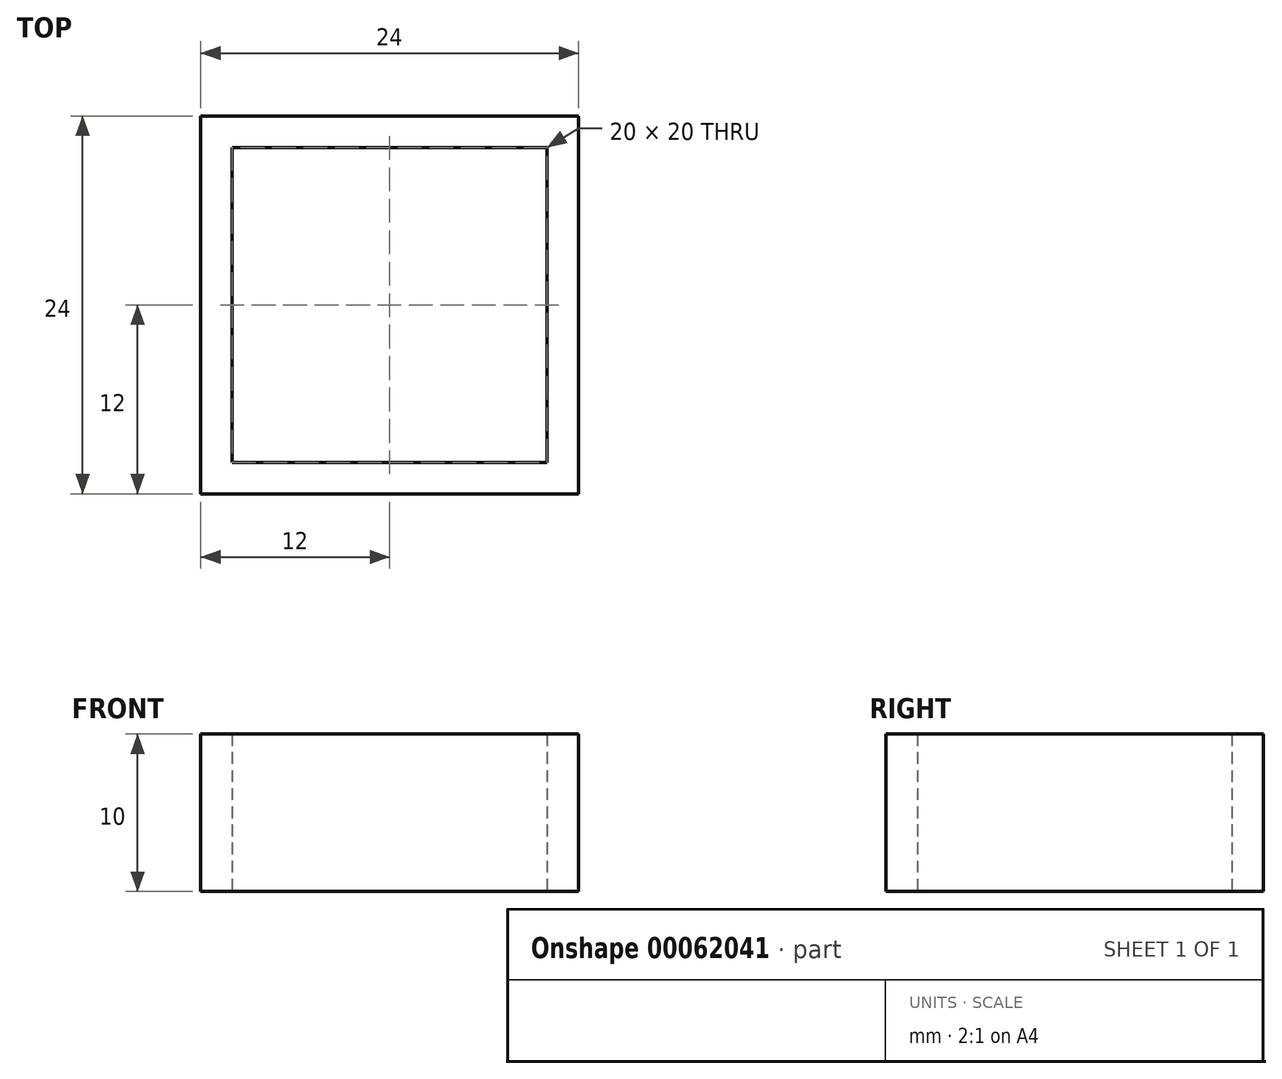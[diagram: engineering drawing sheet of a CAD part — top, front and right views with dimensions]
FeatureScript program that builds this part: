
annotation { "Feature Type Name" : "Feature", "Feature Type Description" : "" }
export const myFeature = defineFeature(function(context is Context, id is Id, definition is map)
    precondition{}
    {
        {
            var Q0;
            Q0=qCreatedBy(makeId("Top.planeOp"),FACE);
            var sketch = newSketch(context, id + "F0", { "sketchPlane" : qUnion([Q0])});
            skLineSegment(sketch, "E0.rect.bottom", {"start": v(10, -10) * mm, "end": v(-10, -10) * mm});
            skLineSegment(sketch, "E0.rect.top", {"start": v(10, 10) * mm, "end": v(-10, 10) * mm});
            skLineSegment(sketch, "E0.rect.left", {"start": v(10, -10) * mm, "end": v(10, 10) * mm});
            skLineSegment(sketch, "E0.rect.right", {"start": v(-10, -10) * mm, "end": v(-10, 10) * mm});
            skPoint(sketch, "E0.rect.middle", {"position": v(0, 0) * mm});
            skLineSegment(sketch, "E1.rect.bottom", {"start": v(12, -12) * mm, "end": v(-12, -12) * mm});
            skLineSegment(sketch, "E1.rect.top", {"start": v(12, 12) * mm, "end": v(-12, 12) * mm});
            skLineSegment(sketch, "E1.rect.left", {"start": v(12, -12) * mm, "end": v(12, 12) * mm});
            skLineSegment(sketch, "E1.rect.right", {"start": v(-12, -12) * mm, "end": v(-12, 12) * mm});
            skSolve(sketch);
        }
        {
            var Q0;
            Q0=makeQuery(id+"F0.imprint","IMPRINT",FACE,{"disambiguationData":[TD([[makeQuery(id+"F0.imprint","IMPRINT",EDGE,{"derivedFrom":sQuery(id+"F0.wireOp",EDGE,"E0.rect.bottom")}),1.0]])]});
            extrude(context, id + "F1", {"entities" : qUnion([Q0]), "depth" : 10 * mm});
        }
    });
